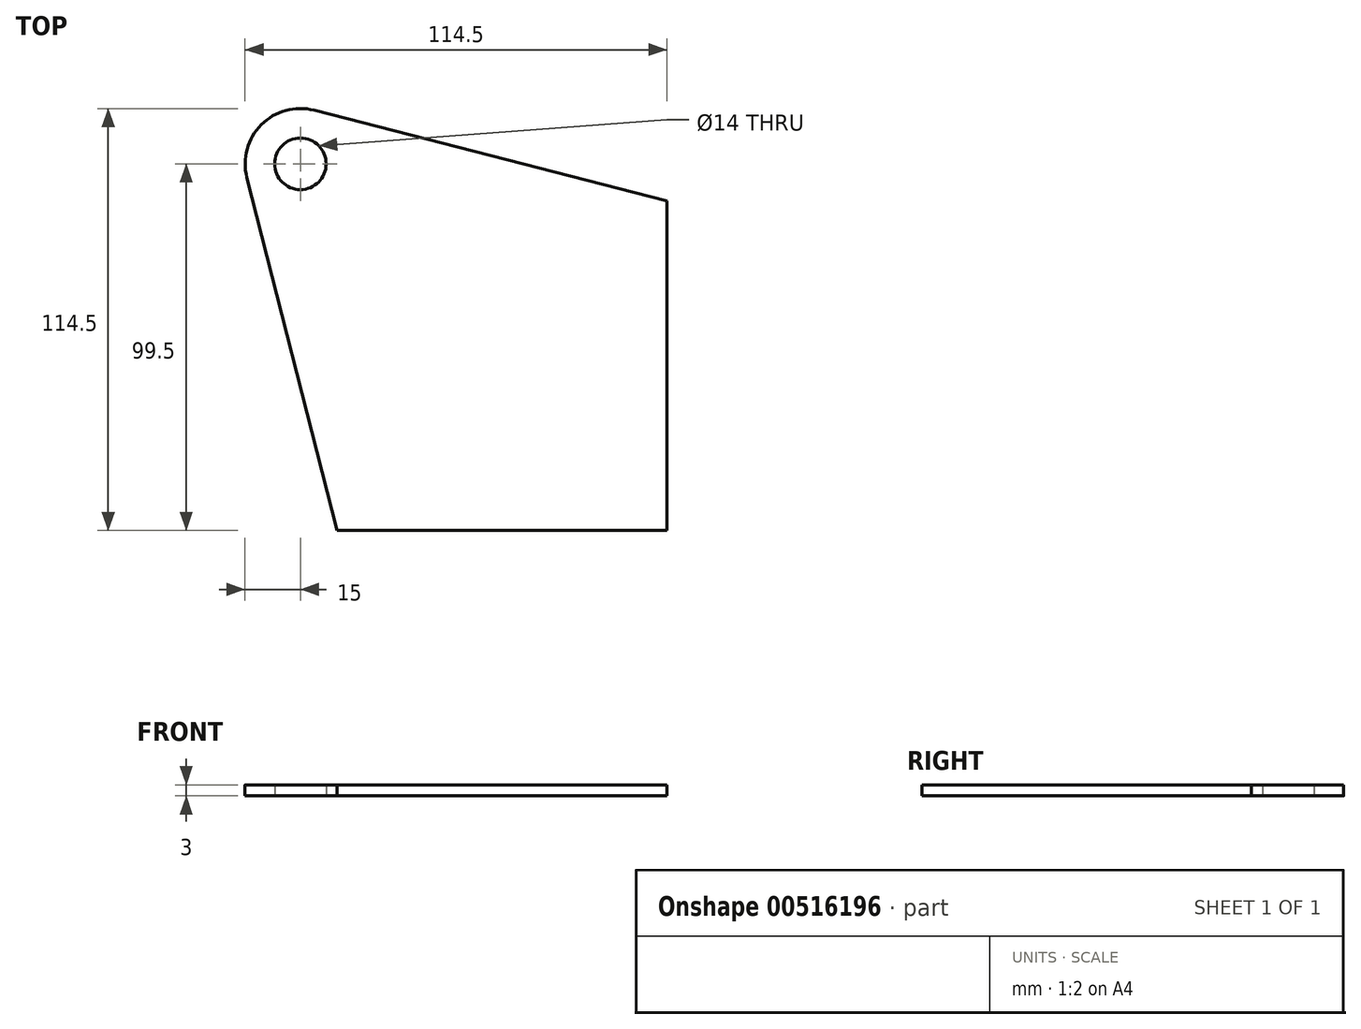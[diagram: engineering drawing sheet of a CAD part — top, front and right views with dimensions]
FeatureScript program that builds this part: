
annotation { "Feature Type Name" : "Feature", "Feature Type Description" : "" }
export const myFeature = defineFeature(function(context is Context, id is Id, definition is map)
    precondition{}
    {
        {
            var Q0;
            Q0=qCreatedBy(makeId("Top.planeOp"),FACE);
            var sketch = newSketch(context, id + "F0", { "sketchPlane" : qUnion([Q0])});
            skLineSegment(sketch, "E0.bottom", {"start": v(-100, 100) * mm, "end": v(100, 100) * mm, "construction": true});
            skLineSegment(sketch, "E0.top", {"start": v(-100, -100) * mm, "end": v(100, -100) * mm, "construction": true});
            skLineSegment(sketch, "E0.left", {"start": v(-100, 100) * mm, "end": v(-100, -100) * mm, "construction": true});
            skLineSegment(sketch, "E0.right", {"start": v(100, 100) * mm, "end": v(100, -100) * mm, "construction": true});
            skPoint(sketch, "E0.middle", {"position": v(0, 0) * mm});
            skCircle(sketch, "E1", {"center": v(-100, 100) * mm, "radius": 7 * mm, "construction": true});
            skCircle(sketch, "E2", {"center": v(100, 100) * mm, "radius": 7 * mm, "construction": true});
            skCircle(sketch, "E3", {"center": v(100, -100) * mm, "radius": 7 * mm, "construction": true});
            skCircle(sketch, "E4", {"center": v(-100, -100) * mm, "radius": 7 * mm, "construction": true});
            skSolve(sketch);
        }
        {
            var Q0;
            Q0=qCreatedBy(makeId("Top.planeOp"),FACE);
            var sketch = newSketch(context, id + "F1", { "sketchPlane" : qUnion([Q0])});
            skCircle(sketch, "E5.0", {"center": v(-100, 100) * mm, "radius": 7 * mm});
            skCircle(sketch, "E6.0", {"center": v(100, 100) * mm, "radius": 7 * mm});
            skCircle(sketch, "E7.0", {"center": v(100, -100) * mm, "radius": 7 * mm});
            skCircle(sketch, "E8.0", {"center": v(-100, -100) * mm, "radius": 7 * mm});
            skCircle(sketch, "E9", {"center": v(-100, 100) * mm, "radius": 15 * mm});
            skLineSegment(sketch, "E10", {"start": v(-96.28, 114.53) * mm, "end": v(-0.5, 90) * mm});
            skLineSegment(sketch, "E11", {"start": v(-0.5, 90) * mm, "end": v(-0.5, 0.5) * mm});
            skLineSegment(sketch, "E12", {"start": v(-0.5, 0.5) * mm, "end": v(-90, 0.5) * mm});
            skLineSegment(sketch, "E13", {"start": v(-90, 0.5) * mm, "end": v(-114.53, 96.28) * mm});
            skSolve(sketch);
        }
        {
            var Q0;
            {var subQ0=sQuery(id+"F1.wireOp",EDGE,"E10");Q0=makeQuery(id+"F1.imprint","IMPRINT",FACE,{"disambiguationData":[TD([[makeQuery(id+"F1.imprint","IMPRINT",EDGE,{"derivedFrom":subQ0}),-1.0]])]});}
            var Q1;
            Q1=makeQuery(id+"F1.imprint","IMPRINT",FACE,{"disambiguationData":[TD([[makeQuery(id+"F1.imprint","IMPRINT",EDGE,{"derivedFrom":sQuery(id+"F1.wireOp",EDGE,"E5.0")}),-1.0]])]});
            extrude(context, id + "F2", {"entities" : qUnion([Q0, Q1]), "depth" : 3 * mm, "offsetDistance" : 25 * mm});
        }
    });
